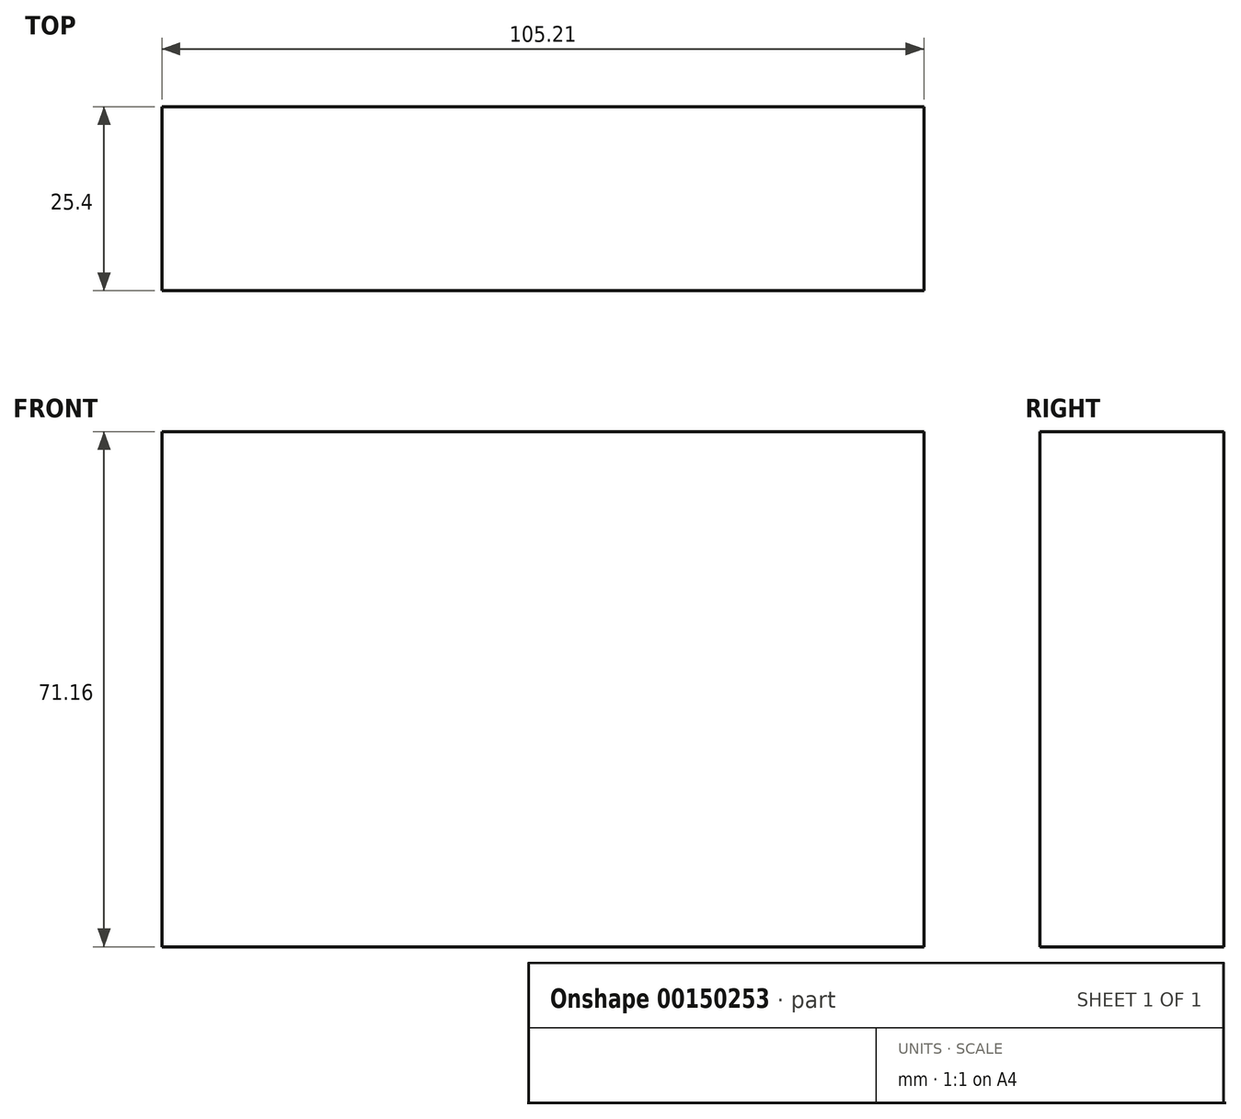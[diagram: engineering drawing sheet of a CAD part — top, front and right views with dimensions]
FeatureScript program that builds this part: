
annotation { "Feature Type Name" : "Feature", "Feature Type Description" : "" }
export const myFeature = defineFeature(function(context is Context, id is Id, definition is map)
    precondition{}
    {
        {
            var Q0;
            Q0=qCreatedBy(makeId("Front.planeOp"),FACE);
            var sketch = newSketch(context, id + "F0", { "sketchPlane" : qUnion([Q0])});
            skLineSegment(sketch, "E0.bottom", {"start": v(-56.1, 37.07) * mm, "end": v(49.1, 37.07) * mm});
            skLineSegment(sketch, "E0.top", {"start": v(-56.1, -34.09) * mm, "end": v(49.1, -34.09) * mm});
            skLineSegment(sketch, "E0.left", {"start": v(-56.1, 37.07) * mm, "end": v(-56.1, -34.09) * mm});
            skLineSegment(sketch, "E0.right", {"start": v(49.1, 37.07) * mm, "end": v(49.1, -34.09) * mm});
            skSolve(sketch);
        }
        {
            var Q0;
            Q0 = qSketchRegion(id + "F0", true);
            var Q1;
            Q1=makeQuery(id+"F0.imprint","IMPRINT",FACE,{"disambiguationData":[TD([[makeQuery(id+"F0.imprint","IMPRINT",EDGE,{"derivedFrom":sQuery(id+"F0.wireOp",EDGE,"E0.bottom")}),-1.0]])]});
            extrude(context, id + "F1", {"entities" : qUnion([Q0, Q1]), "depth" : 25.4 * mm});
        }
    });
